# Revit family: Haworth_BuzziDesk_FlipFlop_Slider
name_source: partatom
category: Furniture
revit_build: Autodesk Revit 2018 (Build: 20170223_1515(x64)
units: mm (PartAtom-declared; Revit-internal decimal feet)

## family parameters
Always vertical = Yes
Cut with Voids When Loaded = No
OmniClass Number = 23.40.70.14.64.21
OmniClass Title = Systems Furniture
Room Calculation Point = No
Shared = No
Work Plane-Based = No

## types (4) — shared parameters
Actual Mounting Height = 29 5/8"
Actual Width = 78 189/256"
Assembly Code = E2020200
Custom Size = No
Manufacturer = Haworth
Max. Width = 78 189/256"
Midsection Widths = 31.5, 39.37, 47.24, 55.12, 62.99, 70.87, 78.74 in
Min. Width = 31 1/2"
Model = HCBZ-DFS
Revision Number = 1
Size = Verify Final Dim. w/ Haworth
URL = http://www.haworth.com
URL - Product = https://www.haworth.com
Warranty = http://www.haworth.com
Width = 78 189/256"

## per-type parameters (varying)
| type | Actual Depth | Actual Height | Description | High | Large | Low | Small |
| HCBZ-DFS1 - Low Screen - Small Sides | 14 195/256" | 13 25/32" | Haworth BuzziDesk FlipFlop - Low Screen - Small Sides | No | No | Yes | Yes |
| HCBZ-DFS2 - High Screen - Small Sides | 14 195/256" | 19 177/256" | Haworth BuzziDesk FlipFlop - High Screen - Small Sides | Yes | No | No | Yes |
| HCBZ-DFS1 - Low Screen - Large Sides | 19 177/256" | 13 25/32" | Haworth BuzziDesk FlipFlop - Low Screen - Large Sides | No | Yes | Yes | No |
| HCBZ-DFS2 - High Screen - Large Sides | 19 177/256" | 19 177/256" | Haworth BuzziDesk FlipFlop - High Screen - Large Sides | Yes | Yes | No | No |

## geometry (parser evidence)
native form markers: Sweep x5
no freeform markers — native parametric forms only
